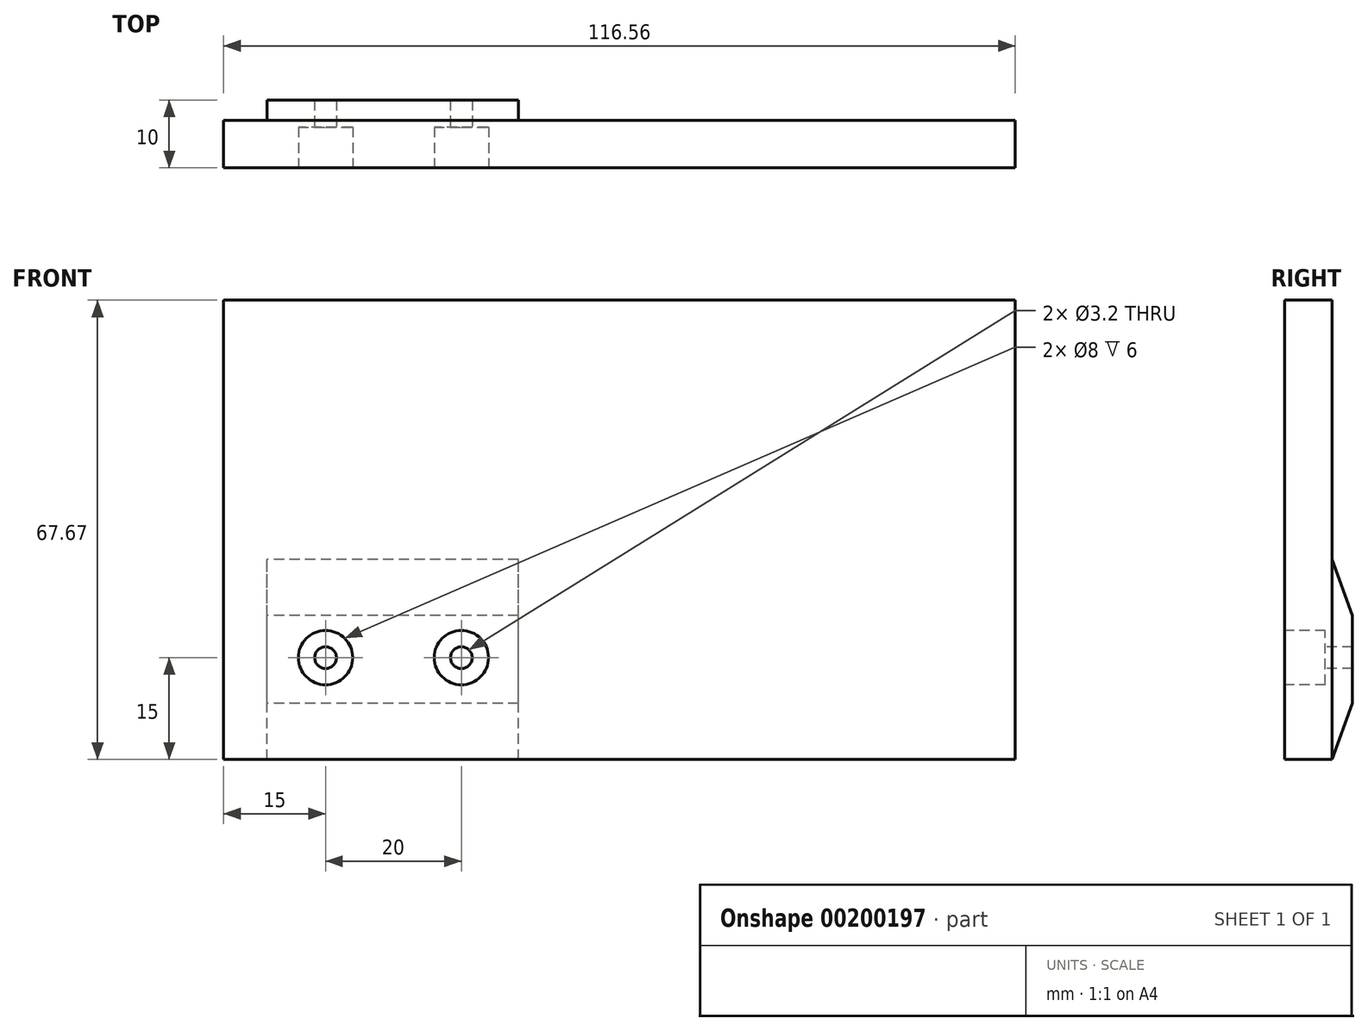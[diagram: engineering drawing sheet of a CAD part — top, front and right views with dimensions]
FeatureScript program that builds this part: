
annotation { "Feature Type Name" : "Feature", "Feature Type Description" : "" }
export const myFeature = defineFeature(function(context is Context, id is Id, definition is map)
    precondition{}
    {
        {
            var Q0;
            Q0=qCreatedBy(makeId("Front.planeOp"),FACE);
            var sketch = newSketch(context, id + "F0", { "sketchPlane" : qUnion([Q0])});
            skLineSegment(sketch, "E0.bottom", {"start": v(0, 0) * mm, "end": v(116.56, 0) * mm});
            skLineSegment(sketch, "E0.top", {"start": v(0, 67.67) * mm, "end": v(116.56, 67.67) * mm});
            skLineSegment(sketch, "E0.left", {"start": v(0, 0) * mm, "end": v(0, 67.67) * mm});
            skLineSegment(sketch, "E0.right", {"start": v(116.56, 0) * mm, "end": v(116.56, 67.67) * mm});
            skSolve(sketch);
        }
        {
            var Q0;
            Q0 = qSketchRegion(id + "F0", true);
            extrude(context, id + "F1", {"entities" : qUnion([Q0]), "depth" : 7 * mm});
        }
        {
            var Q0;
            Q0=makeQuery(id+"F1.opExtrude","CAP_FACE",FACE,{"disambiguationData":[OSD([sQuery(id+"F0.wireOp",EDGE,"E0.bottom"),sQuery(id+"F0.wireOp",EDGE,"E0.top"),sQuery(id+"F0.wireOp",EDGE,"E0.left"),sQuery(id+"F0.wireOp",EDGE,"E0.right")])],"isStart":false});
            var sketch = newSketch(context, id + "F2", { "sketchPlane" : qUnion([Q0])});
            skCircle(sketch, "E1", {"center": v(15, 15) * mm, "radius": 1.6 * mm});
            skCircle(sketch, "E2", {"center": v(15, 15) * mm, "radius": 4 * mm});
            skCircle(sketch, "E3", {"center": v(35, 15) * mm, "radius": 1.6 * mm});
            skCircle(sketch, "E4", {"center": v(35, 15) * mm, "radius": 4 * mm});
            skSolve(sketch);
        }
        {
            var Q0;
            Q0=makeQuery(id+"F1.opExtrude","SWEPT_FACE",FACE,{"disambiguationData":[OSD([sQuery(id+"F0.wireOp",EDGE,"E0.left")])]});
            var sketch = newSketch(context, id + "F3", { "sketchPlane" : qUnion([Q0])});
            skLineSegment(sketch, "E5", {"start": v(0, 0) * mm, "end": v(-3, 8.24) * mm});
            skLineSegment(sketch, "E6", {"start": v(-3, 8.24) * mm, "end": v(-3, 21.24) * mm});
            skLineSegment(sketch, "E7", {"start": v(-3, 21.24) * mm, "end": v(0, 29.48) * mm});
            skLineSegment(sketch, "E8", {"start": v(0, 29.48) * mm, "end": v(0, 0) * mm});
            skSolve(sketch);
        }
        {
            var Q0;
            Q0 = qSketchRegion(id + "F3", true);
            extrude(context, id + "F4", {"entities" : qUnion([Q0]), "operationType" : NewBodyOperationType.ADD, "oppositeDirection" : true, "depth" : 43.4 * mm, "hasSecondDirection" : true, "secondDirectionOppositeDirection" : true, "secondDirectionDepth" : 6.4 * mm});
        }
        {
            var Q0;
            Q0=makeQuery(id+"F2.imprint","IMPRINT",FACE,{"disambiguationData":[TD([[makeQuery(id+"F2.imprint","IMPRINT",EDGE,{"derivedFrom":sQuery(id+"F2.wireOp",EDGE,"E1")}),1.0]])]});
            var Q1;
            Q1=makeQuery(id+"F2.imprint","IMPRINT",FACE,{"disambiguationData":[TD([[makeQuery(id+"F2.imprint","IMPRINT",EDGE,{"derivedFrom":sQuery(id+"F2.wireOp",EDGE,"E3")}),1.0]])]});
            extrude(context, id + "F5", {"entities" : qUnion([Q0, Q1]), "operationType" : NewBodyOperationType.REMOVE, "endBound" : BoundingType.THROUGH_ALL, "oppositeDirection" : true, "depth" : 25 * mm});
        }
        {
            var Q0;
            Q0=makeQuery(id+"F2.imprint","IMPRINT",FACE,{"disambiguationData":[TD([[makeQuery(id+"F2.imprint","IMPRINT",EDGE,{"derivedFrom":sQuery(id+"F2.wireOp",EDGE,"E1")}),-1.0]])]});
            var Q1;
            Q1=makeQuery(id+"F2.imprint","IMPRINT",FACE,{"disambiguationData":[TD([[makeQuery(id+"F2.imprint","IMPRINT",EDGE,{"derivedFrom":sQuery(id+"F2.wireOp",EDGE,"E3")}),-1.0]])]});
            extrude(context, id + "F6", {"entities" : qUnion([Q0, Q1]), "operationType" : NewBodyOperationType.REMOVE, "oppositeDirection" : true, "depth" : 6 * mm});
        }
    });
